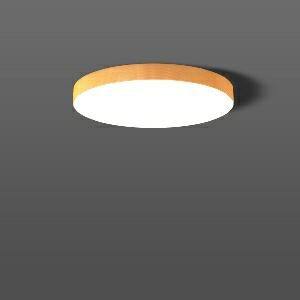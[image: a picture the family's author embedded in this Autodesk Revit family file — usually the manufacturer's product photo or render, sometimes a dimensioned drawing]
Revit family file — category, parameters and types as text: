
# Revit family: flatliner_slim_312283_002_76_4183
name_source: partatom
category: Lighting Fixtures
units: mm (PartAtom-declared; Revit-internal decimal feet)

## family parameters
Cut with Voids When Loaded = No
Host = Face
Light Source = No
Part Type = Normal
Room Calculation Point = No
Round Connector Dimension = Use Diameter
Shared = No

## types (1)
- 982557.002 (1 x LED Modul 830, 2200 lm, 3000)
    Apparent Load = 31 VA
    CIE Flux Codes = 45 76 94 95 100
    Color Rendering = 80
    Color Temperature = 3000
    Default Elevation = 1800 mm
    Description = Series: FLATLINER SLIM
Decorative ceiling luminaire for interior decoration. Base luminaire prepared for the installation of fabric lampshade. Base: metal, white, powder-coated. TouchDim sensor capable. Light and/or presence sensors can be integrated. Modular design: with the basic luminaire, a cylindrical fabric lampshade with a polycarbonate satin-finish diffuser must always be ordered separately. Fabric lampshade and diffuser can be assembled without the use of tools. 
Colour: white
Diameter: 418 mm
Height: 34 mm
Lamp: LED exchangeable
Socket: without socket
Colour temperature: 3000K
Colour rendering index (CRI): 83
System power: 31 W
Rated luminous flux: 2200 lm
Beam angle Down: 117°
Luminous efficiency: 71 lm/W
Control gear: AC power, DALI dimmable
Protection class: I
Type of protection: IP 20
    Height = 34 mm  [stored 0.111549 ft]
    Lamp = 1 x LED Modul 830
    Lamp Light Flux = 2200 lm
    Lamp count = 1
    Length = 418 mm
    Lifetime = 50000 h
    Luminous efficacy = 71 lm/W
    Manufacturer = RZB
    ModVariant = No
    Model = 312283.002.76
    Mounting Place = Ceiling
    Mounting Type = Surface mounted
    Number of Poles = 1
    OnlyDefault = Yes
    Power Factor = 1
    Product Name = FLATLINER SLIM
    Product group = Surface mounted ceiling Fabric lampshade luminaires
    ProductGroupID = 313
    Protection Class = Protection class I
    Protection Degree = IP 20
    RLX_Detail_Level = 1
    RLX_Emergency_Light_Flux = 0 lm
    RLX_Emergency_Type = 0
    RLX_Emergency_Type_DB = No
    RlxData = <blob elided: 25725 chars, md5=f8782f91>
    Socket = socket
    Standby Power = 0 W
    System Light Flux = 2200 lm
    System Power = 31 W
    Type Image = 312287.002_982442.0063_982444.002.jpg
    URL = http://relux.com
    VarID = 982557_002_b87f
    Voltage = 230 V
    Voltage Range = 220-240 V
    Weight = 0.00 kg
    Width = 0 mm  [stored 0 ft]

note: [stored X ft] marks values corroborated as IEEE doubles in the binary element streams (Revit-internal decimal feet)

## geometry (parser evidence)
native form markers: Blend x4, Sweep x14
no freeform markers — native parametric forms only
